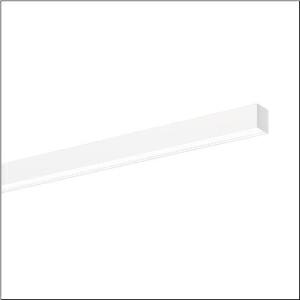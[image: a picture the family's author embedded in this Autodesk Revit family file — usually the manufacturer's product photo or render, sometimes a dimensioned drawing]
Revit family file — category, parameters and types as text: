
# Revit family: silica_r__21_51mx20da42wb_78eb
name_source: partatom
category: Lighting Fixtures
units: mm (PartAtom-declared; Revit-internal decimal feet)

## family parameters
Cut with Voids When Loaded = No
Host = Face
Light Source = No
Part Type = Normal
Room Calculation Point = No
Round Connector Dimension = Use Diameter
Shared = No

## types (1)
- --- (1 x LED, 2400 lm, 15.2 W, 4000K)
    Apparent Load = 15 VA
    CIE Flux Codes = 48 79 96 100 100
    Color Rendering = 80
    Color Temperature = 4000K
    Default Elevation = 1800 mm
    Description = Silica® 21, office luminaire, primary optical cover: cover, of PMMA, opal, light emission: direct distribution, primary light characteristic: symmetric, installation type: surface-mounted, LED, rated luminous flux: 2.400lm, luminous efficacy: 158lm/W, light colour: 840, colour temperature: 4000K, with terminal, 3+2-pole, max. 2.5mm², mains connection: 220..240V, AC, 50/60Hz, rated input power: 15.2W, luminaire housing, of aluminium, traffic white (RAL 9016), length: 1.204mm, width: 53mm, height: 53mm, protection rating (complete): IP20, insulation class (complete): insulation class I (protective earthing), certification: CE, permissible operating ambient temperature: 0..+35°C, standard: EN 50419, packaging unit: 1 piece
    Height = 0 mm  [stored 0 ft]
    Lamp = 1 x LED
    Lamp Light Flux = 2400 lm
    Lamp Power = 15.2 W
    Lamp count = 1
    Length = 1204 mm
    Luminous efficacy = 158 lm/W
    Manufacturer = Siteco
    ModVariant = No
    Model = 51MX20DA42WB
    Mounting Place = Ceiling
    Mounting Type = Recessed
    Number of Poles = 1
    OnlyDefault = Yes
    Power Factor = 1
    Product Name = Silica® 21
    Product group = office luminaire | ceiling recessed
    ProductGroupID = 400
    Protection Class = Protection class I
    Protection Degree = IP 20
    RLX_Detail_Level = 1
    RLX_Emergency_Light_Flux = 0 lm
    RLX_Emergency_Type = 0
    RLX_Emergency_Type_DB = No
    RlxData = <blob elided: 23741 chars, md5=7fbecd13>
    Socket = socket
    Standby Power = 0 W
    System Light Flux = 2400 lm
    System Power = 15 W
    Type Comments = factory setting: luminous flux: 100 % | dim-lin: 254 | 218 mA
    Type Image = l_1335877.jpg
    URL = http://relux.com
    VarID = @adj_087337
    Voltage = 0 V
    Weight = 0.00 kg
    Width = 53 mm

note: [stored X ft] marks values corroborated as IEEE doubles in the binary element streams (Revit-internal decimal feet)

## geometry (parser evidence)
native form markers: Blend x4, Sweep x13
no freeform markers — native parametric forms only
